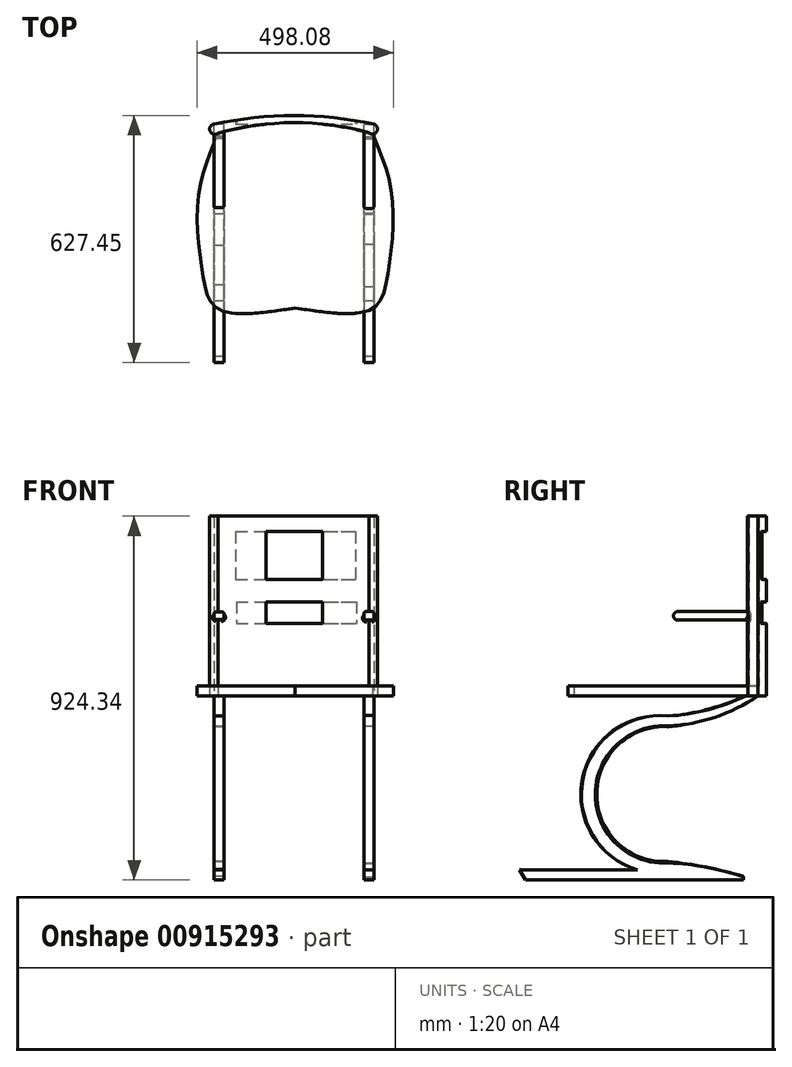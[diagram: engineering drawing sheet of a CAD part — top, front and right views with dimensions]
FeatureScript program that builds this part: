
annotation { "Feature Type Name" : "Feature", "Feature Type Description" : "" }
export const myFeature = defineFeature(function(context is Context, id is Id, definition is map)
    precondition{}
    {
        {
            var Q0;
            Q0=qCreatedBy(makeId("Top.planeOp"),FACE);
            var sketch = newSketch(context, id + "F0", { "sketchPlane" : qUnion([Q0])});
            skArc(sketch, "E0", {"start": v(0, 0) * mm, "mid": v(-203.2, 21.53) * mm, "end": v(-406.4, 0) * mm});
            skArc(sketch, "E1", {"start": v(-12.74, -21.97) * mm, "mid": v(-204.43, 3.64) * mm, "end": v(-395.95, -23.15) * mm});
            skArc(sketch, "E2", {"start": v(-406.4, 0) * mm, "mid": v(-416.29, -18.4) * mm, "end": v(-395.95, -23.15) * mm});
            skArc(sketch, "E3", {"start": v(-12.74, -21.97) * mm, "mid": v(6.94, -18.7) * mm, "end": v(0, 0) * mm});
            skLineSegment(sketch, "E4", {"start": v(-406.4, 0) * mm, "end": v(0, 0) * mm, "construction": true});
            skLineSegment(sketch, "E5", {"start": v(-200.03, 3.64) * mm, "end": v(-200.03, -453.56) * mm, "construction": true});
            skPoint(sketch, "E5.startSnap0", {"position": v(-204.43, 3.64) * mm});
            skFitSpline(sketch, "E6", {"points": [v(-395.95, -23.15) * mm, v(-446.34, -185.32) * mm, v(-435.29, -380.68) * mm, v(-395.95, -469.14) * mm, v(-200.03, -467.3) * mm], "startDerivative": vector(-254.03, -599.98) * mm, "endDerivative": vector(861.36, 130.72) * mm});
            skFitSpline(sketch, "E7.MirrorCS", {"points": [v(-4.11, -23.15) * mm, v(46.28, -185.32) * mm, v(35.22, -380.68) * mm, v(-4.11, -469.14) * mm, v(-200.03, -467.3) * mm], "startDerivative": vector(254.03, -599.98) * mm, "endDerivative": vector(-861.36, 130.72) * mm});
            skSolve(sketch);
        }
        {
            var Q0;
            {var subQ3=sQuery(id+"F0.wireOp",EDGE,"E0");Q0=makeQuery(id+"F0.imprint","IMPRINT",FACE,{"disambiguationData":[TD([[makeQuery(id+"F0.imprint","IMPRINT",EDGE,{"derivedFrom":subQ3}),1.0]])]});}
            extrude(context, id + "F1", {"entities" : qUnion([Q0]), "depth" : 457.2 * mm, "offsetDistance" : 25.4 * mm});
        }
        {
            var Q0;
            {var subQ0=sQuery(id+"F0.wireOp",EDGE,"E1");Q0=makeQuery(id+"F0.imprint","IMPRINT",FACE,{"disambiguationData":[TD([[makeQuery(id+"F0.imprint","IMPRINT",EDGE,{"derivedFrom":subQ0}),1.0]])]});}
            extrude(context, id + "F2", {"entities" : qUnion([Q0]), "operationType" : NewBodyOperationType.ADD, "depth" : 25.4 * mm, "offsetDistance" : 25.4 * mm});
        }
        {
            var Q0;
            Q0=qCreatedBy(makeId("Right.planeOp"),FACE);
            var sketch = newSketch(context, id + "F3", { "sketchPlane" : qUnion([Q0])});
            skLineSegment(sketch, "E8", {"start": v(0, 0) * mm, "end": v(0, -457.2) * mm, "construction": true});
            skArc(sketch, "E9", {"start": v(-228.2, -76.13) * mm, "mid": v(-412.66, -251.43) * mm, "end": v(-225.75, -424.13) * mm});
            skArc(sketch, "E10", {"start": v(-228.2, -76.13) * mm, "mid": v(-108.8, -53.96) * mm, "end": v(0, 0) * mm});
            skArc(sketch, "E11", {"start": v(-36.49, -459.54) * mm, "mid": v(-129.9, -435.28) * mm, "end": v(-225.75, -424.13) * mm});
            skLineSegment(sketch, "E12", {"start": v(0, 0) * mm, "end": v(-30.4, 0) * mm});
            skArc(sketch, "E13", {"start": v(-228.2, -50.73) * mm, "mid": v(-126.69, -35.17) * mm, "end": v(-30.4, 0.55) * mm});
            skArc(sketch, "E14", {"start": v(-228.2, -50.73) * mm, "mid": v(-447.99, -250.78) * mm, "end": v(-226.83, -449.32) * mm});
            skLineSegment(sketch, "E15", {"start": v(0, -457.2) * mm, "end": v(-369.88, -457.2) * mm, "construction": true});
            skLineSegment(sketch, "E16", {"start": v(-305.2, -441.97) * mm, "end": v(-605.92, -441.97) * mm});
            skLineSegment(sketch, "E17", {"start": v(-605.92, -441.97) * mm, "end": v(-589.52, -466.88) * mm});
            skLineSegment(sketch, "E18", {"start": v(-589.52, -466.88) * mm, "end": v(-36.49, -466.88) * mm});
            skLineSegment(sketch, "E19", {"start": v(-36.49, -466.88) * mm, "end": v(-36.49, -459.54) * mm});
            skLineSegment(sketch, "E20", {"start": v(0, 0) * mm, "end": v(-30.4, 0.55) * mm});
            skLineSegment(sketch, "E21", {"start": v(0, 192.88) * mm, "end": v(-203.2, 192.88) * mm});
            skLineSegment(sketch, "E22", {"start": v(0, 214.47) * mm, "end": v(-203.2, 214.47) * mm});
            skArc(sketch, "E23", {"start": v(-203.2, 214.47) * mm, "mid": v(-214, 203.68) * mm, "end": v(-203.2, 192.88) * mm});
            skLineSegment(sketch, "E24", {"start": v(0, 192.88) * mm, "end": v(0, 26.3) * mm, "construction": true});
            skLineSegment(sketch, "E25", {"start": v(0, 214.47) * mm, "end": v(0, 192.88) * mm});
            skSolve(sketch);
        }
        {
            var Q0;
            Q0 = qSketchRegion(id + "F3", true);
            extrude(context, id + "F4", {"entities" : qUnion([Q0]), "operationType" : NewBodyOperationType.ADD, "oppositeDirection" : true, "depth" : 25.4 * mm, "offsetDistance" : 25.4 * mm});
        }
        {
            var Q0;
            Q0=qCreatedBy(makeId("Right.planeOp"),FACE);
            cPlane(context, id + "F5", {"entities" : qUnion([Q0]), "cplaneType" : CPlaneType.OFFSET, "offset" : 406.4 * mm, "oppositeDirection" : true, "width" : 152.4 * mm, "height" : 152.4 * mm});
        }
        {
            var Q0;
            Q0=qCreatedBy(id+"F5.planeOp",FACE);
            var sketch = newSketch(context, id + "F6", { "sketchPlane" : qUnion([Q0])});
            skLineSegment(sketch, "E26", {"start": v(-25.36, 0) * mm, "end": v(0, 0) * mm});
            skLineSegment(sketch, "E27.bottom", {"start": v(0, 213.74) * mm, "end": v(-203.2, 213.74) * mm});
            skLineSegment(sketch, "E27.top", {"start": v(0, 194.8) * mm, "end": v(-203.2, 194.8) * mm});
            skLineSegment(sketch, "E27.left", {"start": v(0, 213.74) * mm, "end": v(0, 194.8) * mm});
            skArc(sketch, "E28", {"start": v(-203.2, 213.74) * mm, "mid": v(-212.67, 204.27) * mm, "end": v(-203.2, 194.8) * mm});
            skLineSegment(sketch, "E29", {"start": v(0, 194.8) * mm, "end": v(0, 0) * mm, "construction": true});
            skLineSegment(sketch, "E30", {"start": v(0, 0) * mm, "end": v(-31.54, 0) * mm});
            skArc(sketch, "E31", {"start": v(-229.06, -78.04) * mm, "mid": v(-109.86, -52.72) * mm, "end": v(0, 0) * mm});
            skArc(sketch, "E32", {"start": v(-228.76, -51.42) * mm, "mid": v(-127.98, -34.03) * mm, "end": v(-31.54, 0) * mm});
            skArc(sketch, "E33", {"start": v(-228.76, -51.42) * mm, "mid": v(-449.45, -249.57) * mm, "end": v(-228.76, -447.71) * mm});
            skArc(sketch, "E34", {"start": v(-229.06, -78.04) * mm, "mid": v(-409.06, -249.46) * mm, "end": v(-228.76, -420.57) * mm});
            skArc(sketch, "E35", {"start": v(-36.62, -458.41) * mm, "mid": v(-131.75, -434.73) * mm, "end": v(-228.76, -420.57) * mm});
            skLineSegment(sketch, "E36", {"start": v(-36.62, -458.41) * mm, "end": v(-36.62, -467.14) * mm});
            skLineSegment(sketch, "E37", {"start": v(-36.62, -467.14) * mm, "end": v(-590.08, -467.14) * mm});
            skLineSegment(sketch, "E38", {"start": v(-605.49, -441.5) * mm, "end": v(-590.08, -467.14) * mm});
            skLineSegment(sketch, "E39", {"start": v(-605.49, -441.5) * mm, "end": v(-308.47, -440.14) * mm});
            skSolve(sketch);
        }
        {
            var Q0;
            Q0 = qSketchRegion(id + "F6", true);
            extrude(context, id + "F7", {"entities" : qUnion([Q0]), "operationType" : NewBodyOperationType.ADD, "depth" : 25.4 * mm, "offsetDistance" : 25.4 * mm});
        }
        {
            var Q0;
            Q0=makeQuery(id+"F7.opExtrude","CAP_EDGE",EDGE,{"disambiguationData":[OSD([sQuery(id+"F6.wireOp",EDGE,"E27.bottom")])],"isStart":true});
            var Q1;
            Q1=makeQuery(id+"F7.opExtrude","CAP_EDGE",EDGE,{"disambiguationData":[OSD([sQuery(id+"F6.wireOp",EDGE,"E27.bottom")])],"isStart":false});
            var Q2;
            Q2=makeQuery(id+"F7.opExtrude","SWEPT_FACE",FACE,{"disambiguationData":[OSD([sQuery(id+"F6.wireOp",EDGE,"E27.top")])]});
            fillet(context, id + "F8", {"entities" : qUnion([Q0, Q1, Q2]), "radius" : 5.08 * mm, "tangentPropagation" : true, "allowEdgeOverflow" : false});
        }
        {
            var Q0;
            Q0=makeQuery(id+"F4.opExtrude","CAP_EDGE",EDGE,{"disambiguationData":[OSD([sQuery(id+"F3.wireOp",EDGE,"E22")])],"isStart":true});
            var Q1;
            Q1=makeQuery(id+"F4.opExtrude","CAP_EDGE",EDGE,{"disambiguationData":[OSD([sQuery(id+"F3.wireOp",EDGE,"E22")])],"isStart":false});
            var Q2;
            Q2=makeQuery(id+"F4.opExtrude","SWEPT_FACE",FACE,{"disambiguationData":[OSD([sQuery(id+"F3.wireOp",EDGE,"E21")])]});
            fillet(context, id + "F9", {"entities" : qUnion([Q0, Q1, Q2]), "radius" : 5.08 * mm, "tangentPropagation" : true, "allowEdgeOverflow" : false});
        }
        {
            var Q0;
            Q0=qCreatedBy(makeId("Front.planeOp"),FACE);
            var sketch = newSketch(context, id + "F10", { "sketchPlane" : qUnion([Q0])});
            skLineSegment(sketch, "E40.bottom", {"start": v(-351.32, 418.2) * mm, "end": v(-46.52, 418.2) * mm});
            skLineSegment(sketch, "E40.top", {"start": v(-351.32, 295.9) * mm, "end": v(-46.52, 295.9) * mm});
            skLineSegment(sketch, "E40.left", {"start": v(-351.32, 418.2) * mm, "end": v(-351.32, 295.9) * mm});
            skLineSegment(sketch, "E40.right", {"start": v(-46.52, 418.2) * mm, "end": v(-46.52, 295.9) * mm});
            skLineSegment(sketch, "E41.bottom", {"start": v(-349.58, 239.33) * mm, "end": v(-44.78, 239.33) * mm});
            skLineSegment(sketch, "E41.top", {"start": v(-349.58, 184.57) * mm, "end": v(-44.78, 184.57) * mm});
            skLineSegment(sketch, "E41.left", {"start": v(-349.58, 239.33) * mm, "end": v(-349.58, 184.57) * mm});
            skLineSegment(sketch, "E41.right", {"start": v(-44.78, 239.33) * mm, "end": v(-44.78, 184.57) * mm});
            skSolve(sketch);
        }
        {
            var Q0;
            Q0 = qSketchRegion(id + "F10", true);
            extrude(context, id + "F11", {"entities" : qUnion([Q0]), "operationType" : NewBodyOperationType.REMOVE, "oppositeDirection" : true, "depth" : 38.1 * mm, "offsetDistance" : 25.4 * mm});
        }
    });
